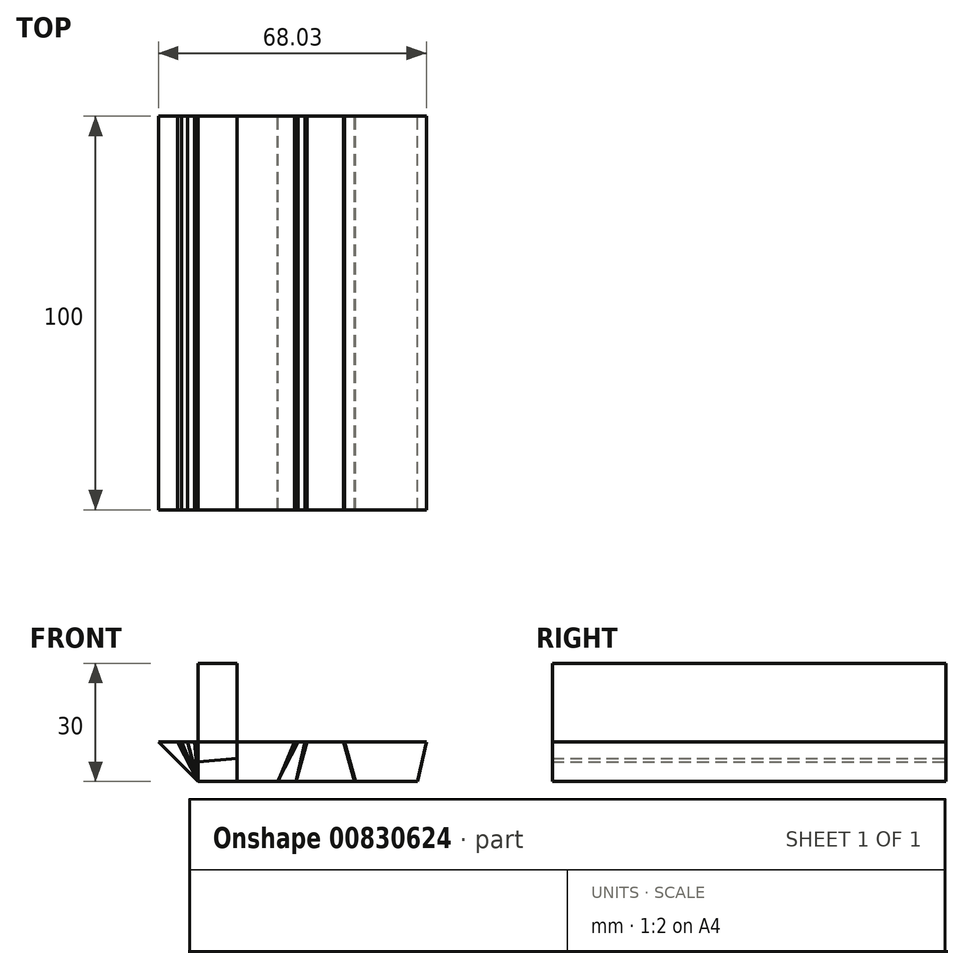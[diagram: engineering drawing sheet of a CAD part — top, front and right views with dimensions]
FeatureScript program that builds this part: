
annotation { "Feature Type Name" : "Feature", "Feature Type Description" : "" }
export const myFeature = defineFeature(function(context is Context, id is Id, definition is map)
    precondition{}
    {
        {
            var Q0;
            Q0=qCreatedBy(makeId("Front.planeOp"),FACE);
            var sketch = newSketch(context, id + "F0", { "sketchPlane" : qUnion([Q0])});
            skLineSegment(sketch, "E0.bottom", {"start": v(0, 0) * mm, "end": v(10, 0) * mm});
            skLineSegment(sketch, "E0.top", {"start": v(0, 30) * mm, "end": v(10, 30) * mm});
            skLineSegment(sketch, "E0.left", {"start": v(0, 0) * mm, "end": v(0, 30) * mm});
            skLineSegment(sketch, "E0.right", {"start": v(10, 0) * mm, "end": v(10, 30) * mm});
            skSolve(sketch);
        }
        {
            var Q0;
            Q0 = qSketchRegion(id + "F0", true);
            extrude(context, id + "F1", {"entities" : qUnion([Q0]), "depth" : 100 * mm, "offsetDistance" : 25 * mm});
        }
        {
            var Q0;
            Q0=qCreatedBy(makeId("Front.planeOp"),FACE);
            var sketch = newSketch(context, id + "F2", { "sketchPlane" : qUnion([Q0])});
            skLineSegment(sketch, "E1.bottom", {"start": v(0, 0) * mm, "end": v(39.74, 0) * mm});
            skLineSegment(sketch, "E1.top", {"start": v(0, 10) * mm, "end": v(37.06, 10) * mm});
            skLineSegment(sketch, "E1.left", {"start": v(0, 0) * mm, "end": v(0, 10) * mm});
            skLineSegment(sketch, "E1.right", {"start": v(39.74, 0) * mm, "end": v(37.06, 10) * mm});
            skSolve(sketch);
        }
        {
            var Q0;
            Q0 = qSketchRegion(id + "F2", true);
            extrude(context, id + "F3", {"entities" : qUnion([Q0]), "depth" : 100 * mm, "offsetDistance" : 25 * mm});
        }
        {
            var Q0;
            Q0=qCreatedBy(makeId("Front.planeOp"),FACE);
            var sketch = newSketch(context, id + "F4", { "sketchPlane" : qUnion([Q0])});
            skLineSegment(sketch, "E2.bottom", {"start": v(0, 0) * mm, "end": v(25, 0) * mm});
            skLineSegment(sketch, "E2.top", {"start": v(-4.14, 10) * mm, "end": v(27.68, 10) * mm});
            skLineSegment(sketch, "E2.left", {"start": v(0, 0) * mm, "end": v(-4.14, 10) * mm});
            skLineSegment(sketch, "E2.right", {"start": v(25, 0) * mm, "end": v(27.68, 10) * mm});
            skSolve(sketch);
        }
        {
            var Q0;
            Q0 = qSketchRegion(id + "F4", true);
            extrude(context, id + "F5", {"entities" : qUnion([Q0]), "depth" : 100 * mm, "offsetDistance" : 25 * mm});
        }
        {
            var Q0;
            Q0=qCreatedBy(makeId("Front.planeOp"),FACE);
            var sketch = newSketch(context, id + "F6", { "sketchPlane" : qUnion([Q0])});
            skLineSegment(sketch, "E3.bottom", {"start": v(0, 0) * mm, "end": v(40, 0) * mm});
            skLineSegment(sketch, "E3.top", {"start": v(-2.68, 10) * mm, "end": v(37.32, 10) * mm});
            skLineSegment(sketch, "E3.left", {"start": v(0, 0) * mm, "end": v(-2.68, 10) * mm});
            skLineSegment(sketch, "E3.right", {"start": v(40, 0) * mm, "end": v(37.32, 10) * mm});
            skSolve(sketch);
        }
        {
            var Q0;
            Q0 = qSketchRegion(id + "F6", true);
            extrude(context, id + "F7", {"entities" : qUnion([Q0]), "depth" : 100 * mm, "offsetDistance" : 25 * mm});
        }
        {
            var Q0;
            Q0=qCreatedBy(makeId("Front.planeOp"),FACE);
            var sketch = newSketch(context, id + "F8", { "sketchPlane" : qUnion([Q0])});
            skLineSegment(sketch, "E4.bottom", {"start": v(0, 0) * mm, "end": v(20.4, 0) * mm});
            skLineSegment(sketch, "E4.top", {"start": v(-10, 10) * mm, "end": v(24.55, 10) * mm});
            skLineSegment(sketch, "E4.left", {"start": v(0, 0) * mm, "end": v(-10, 10) * mm});
            skLineSegment(sketch, "E4.right", {"start": v(20.41, 0) * mm, "end": v(24.55, 10) * mm});
            skSolve(sketch);
        }
        {
            var Q0;
            Q0 = qSketchRegion(id + "F8", true);
            extrude(context, id + "F9", {"entities" : qUnion([Q0]), "depth" : 100 * mm, "offsetDistance" : 25 * mm});
        }
        {
            var Q0;
            Q0=qCreatedBy(makeId("Front.planeOp"),FACE);
            var sketch = newSketch(context, id + "F10", { "sketchPlane" : qUnion([Q0])});
            skLineSegment(sketch, "E5.bottom", {"start": v(0, 0) * mm, "end": v(55.81, 0) * mm});
            skLineSegment(sketch, "E5.top", {"start": v(-10, 10) * mm, "end": v(58.03, 10) * mm});
            skLineSegment(sketch, "E5.left", {"start": v(0, 0) * mm, "end": v(-10, 10) * mm});
            skLineSegment(sketch, "E5.right", {"start": v(55.81, 0) * mm, "end": v(58.03, 10) * mm});
            skSolve(sketch);
        }
        {
            var Q0;
            Q0 = qSketchRegion(id + "F10", true);
            extrude(context, id + "F11", {"entities" : qUnion([Q0]), "depth" : 100 * mm, "offsetDistance" : 25 * mm});
        }
        {
            var Q0;
            Q0=qCreatedBy(makeId("Front.planeOp"),FACE);
            var sketch = newSketch(context, id + "F12", { "sketchPlane" : qUnion([Q0])});
            skLineSegment(sketch, "E6.bottom", {"start": v(0, 0) * mm, "end": v(25, 0) * mm});
            skLineSegment(sketch, "E6.top", {"start": v(-5.2, 10) * mm, "end": v(27.22, 10) * mm});
            skLineSegment(sketch, "E6.left", {"start": v(0, 0) * mm, "end": v(-5.2, 10) * mm});
            skLineSegment(sketch, "E6.right", {"start": v(25, 0) * mm, "end": v(27.22, 10) * mm});
            skSolve(sketch);
        }
        {
            var Q0;
            Q0 = qSketchRegion(id + "F12", true);
            extrude(context, id + "F13", {"entities" : qUnion([Q0]), "depth" : 100 * mm, "offsetDistance" : 25 * mm});
        }
        {
            var Q0;
            Q0=qCreatedBy(makeId("Front.planeOp"),FACE);
            var sketch = newSketch(context, id + "F14", { "sketchPlane" : qUnion([Q0])});
            skLineSegment(sketch, "E7.bottom", {"start": v(0, 0) * mm, "end": v(20.3, 0) * mm});
            skLineSegment(sketch, "E7.top", {"start": v(-0.87, 10) * mm, "end": v(25.5, 10) * mm});
            skLineSegment(sketch, "E7.left", {"start": v(0, 0) * mm, "end": v(-0.87, 10) * mm});
            skLineSegment(sketch, "E7.right", {"start": v(20.3, 0) * mm, "end": v(25.5, 10) * mm});
            skSolve(sketch);
        }
        {
            var Q0;
            Q0 = qSketchRegion(id + "F14", true);
            extrude(context, id + "F15", {"entities" : qUnion([Q0]), "depth" : 100 * mm, "offsetDistance" : 25 * mm});
        }
        {
            var Q0;
            Q0=qCreatedBy(makeId("Front.planeOp"),FACE);
            var sketch = newSketch(context, id + "F16", { "sketchPlane" : qUnion([Q0])});
            skLineSegment(sketch, "E8.bottom", {"start": v(0, 0) * mm, "end": v(10, 0) * mm});
            skLineSegment(sketch, "E8.top", {"start": v(0, 5) * mm, "end": v(10, 5.87) * mm});
            skLineSegment(sketch, "E8.left", {"start": v(0, 0) * mm, "end": v(0, 5) * mm});
            skLineSegment(sketch, "E8.right", {"start": v(10, 0) * mm, "end": v(10, 5.87) * mm});
            skSolve(sketch);
        }
        {
            var Q0;
            Q0 = qSketchRegion(id + "F16", true);
            extrude(context, id + "F17", {"entities" : qUnion([Q0]), "depth" : 100 * mm, "offsetDistance" : 25 * mm});
        }
    });
